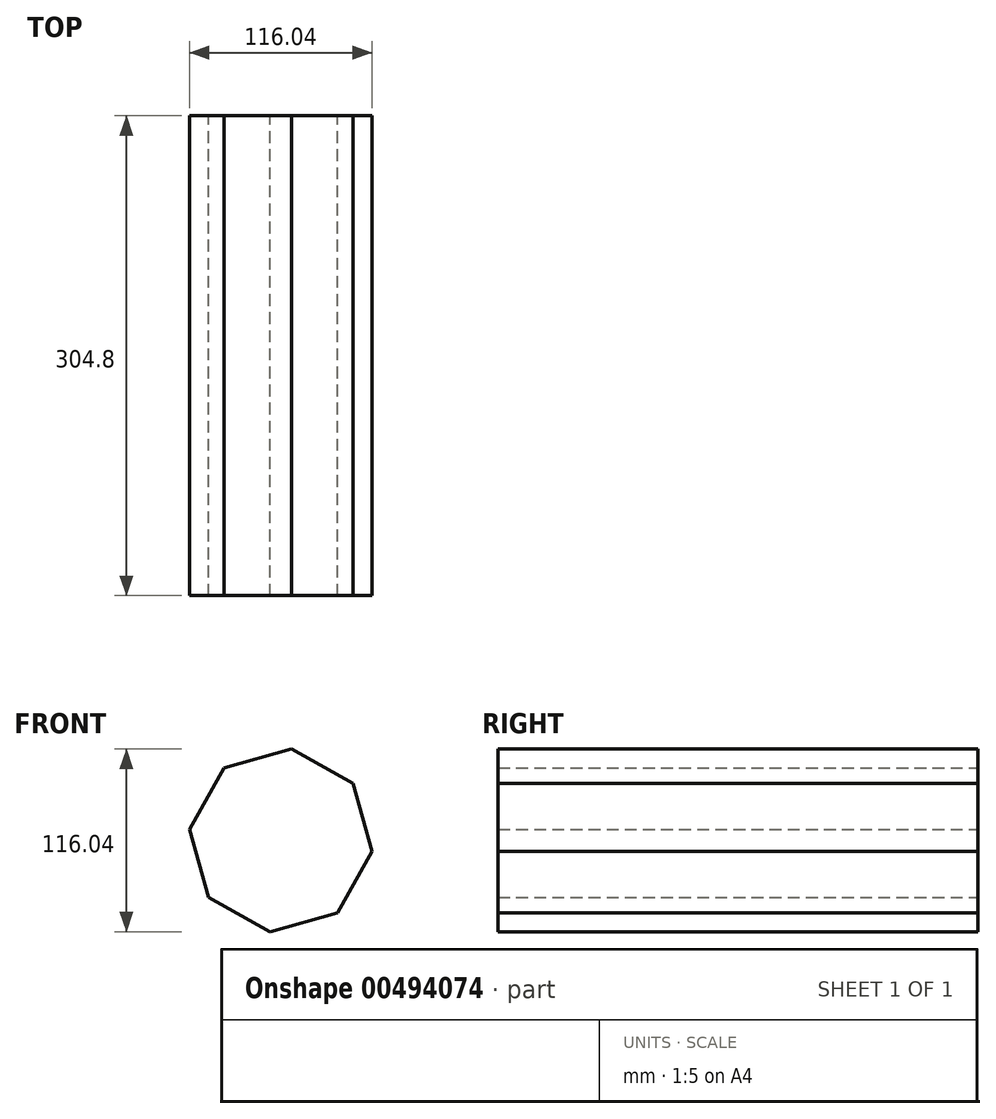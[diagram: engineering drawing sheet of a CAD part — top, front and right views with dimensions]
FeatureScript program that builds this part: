
annotation { "Feature Type Name" : "Feature", "Feature Type Description" : "" }
export const myFeature = defineFeature(function(context is Context, id is Id, definition is map)
    precondition{}
    {
        {
            var Q0;
            Q0=qCreatedBy(makeId("Front.planeOp"),FACE);
            var sketch = newSketch(context, id + "F0", { "sketchPlane" : qUnion([Q0])});
            skCircle(sketch, "E0.cCircle", {"center": v(0, 0) * mm, "radius": 58.43 * mm, "construction": true});
            skLineSegment(sketch, "E0.0", {"start": v(-36.14, 45.9) * mm, "end": v(6.9, 58.02) * mm});
            skLineSegment(sketch, "E0.1", {"start": v(6.9, 58.02) * mm, "end": v(45.9, 36.14) * mm});
            skLineSegment(sketch, "E0.2", {"start": v(45.9, 36.14) * mm, "end": v(58.02, -6.9) * mm});
            skLineSegment(sketch, "E0.3", {"start": v(58.02, -6.9) * mm, "end": v(36.14, -45.9) * mm});
            skLineSegment(sketch, "E0.4", {"start": v(36.14, -45.9) * mm, "end": v(-6.9, -58.02) * mm});
            skLineSegment(sketch, "E0.5", {"start": v(-6.9, -58.02) * mm, "end": v(-45.9, -36.14) * mm});
            skLineSegment(sketch, "E0.6", {"start": v(-45.9, -36.14) * mm, "end": v(-58.02, 6.9) * mm});
            skLineSegment(sketch, "E0.7", {"start": v(-58.02, 6.9) * mm, "end": v(-36.14, 45.9) * mm});
            skSolve(sketch);
        }
        {
            var Q0;
            Q0=makeQuery(id+"F0.imprint","IMPRINT",FACE,{"disambiguationData":[TD([[makeQuery(id+"F0.imprint","IMPRINT",EDGE,{"derivedFrom":sQuery(id+"F0.wireOp",EDGE,"E0.0")}),-1.0]])]});
            extrude(context, id + "F1", {"entities" : qUnion([Q0]), "depth" : 304.8 * mm});
        }
    });
